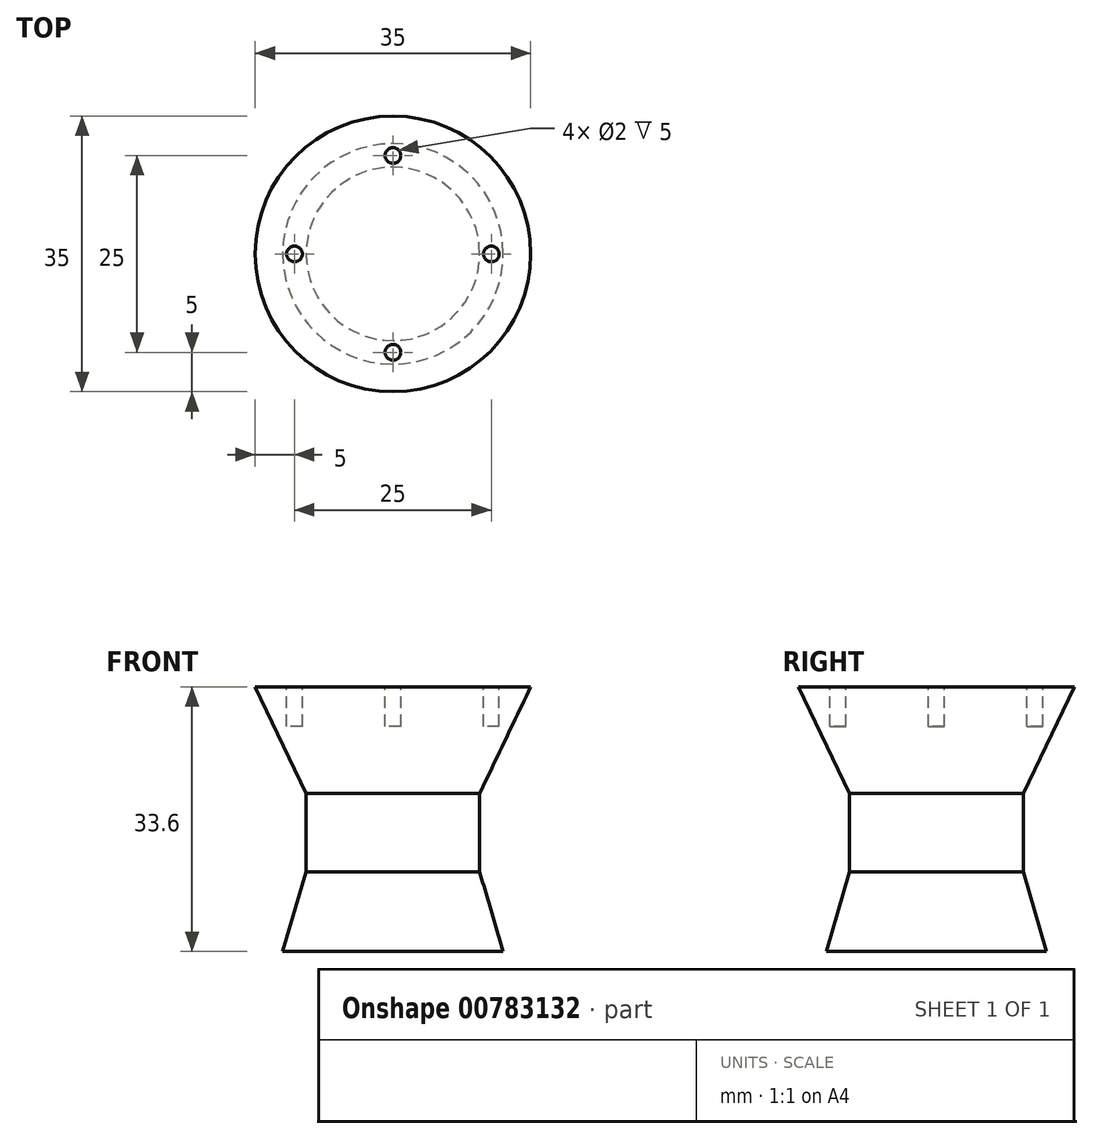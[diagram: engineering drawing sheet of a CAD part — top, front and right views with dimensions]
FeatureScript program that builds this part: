
annotation { "Feature Type Name" : "Feature", "Feature Type Description" : "" }
export const myFeature = defineFeature(function(context is Context, id is Id, definition is map)
    precondition{}
    {
        {
            var Q0;
            Q0=qCreatedBy(makeId("Front.planeOp"),FACE);
            var sketch = newSketch(context, id + "F0", { "sketchPlane" : qUnion([Q0])});
            skLineSegment(sketch, "E0", {"start": v(0, 0) * mm, "end": v(17.5, 0) * mm});
            skLineSegment(sketch, "E1", {"start": v(17.5, 0) * mm, "end": v(11.02, -13.53) * mm});
            skLineSegment(sketch, "E2", {"start": v(0, 0) * mm, "end": v(0, -13.53) * mm});
            skLineSegment(sketch, "E3", {"start": v(0, -13.53) * mm, "end": v(11.02, -13.53) * mm});
            skSolve(sketch);
        }
        {
            var Q0;
            Q0=makeQuery(id+"F0.imprint","IMPRINT",FACE,{"disambiguationData":[TD([[makeQuery(id+"F0.imprint","IMPRINT",EDGE,{"derivedFrom":sQuery(id+"F0.wireOp",EDGE,"E0")}),-1.0]])]});
            var Q1;
            Q1=sQuery(id+"F0.wireOp",EDGE,"E2");
            revolve(context, id + "F1", {"surfaceOperationType" : NewSurfaceOperationType.NEW, "entities" : qUnion([Q0]), "axis" : qUnion([Q1]), "revolveType" : RevolveType.FULL});
        }
        {
            var Q0;
            Q0=makeQuery(id+"F1.opRevolve","SWEPT_FACE",FACE,{"disambiguationData":[OSD([sQuery(id+"F0.wireOp",EDGE,"E0")])]});
            var sketch = newSketch(context, id + "F2", { "sketchPlane" : qUnion([Q0])});
            skCircle(sketch, "E4", {"center": v(0, 0) * mm, "radius": 12.5 * mm, "construction": true});
            skLineSegment(sketch, "E5", {"start": v(-17.5, 0) * mm, "end": v(17.5, 0) * mm, "construction": true});
            skLineSegment(sketch, "E6", {"start": v(0, 17.5) * mm, "end": v(0, -17.5) * mm, "construction": true});
            skCircle(sketch, "E7", {"center": v(12.5, 0) * mm, "radius": 1 * mm});
            skCircle(sketch, "E8", {"center": v(0, 12.5) * mm, "radius": 1 * mm});
            skCircle(sketch, "E9", {"center": v(-12.5, 0) * mm, "radius": 1 * mm});
            skCircle(sketch, "E10", {"center": v(0, -12.5) * mm, "radius": 1 * mm});
            skSolve(sketch);
        }
        {
            var Q0;
            Q0=makeQuery(id+"F2.imprint","IMPRINT",FACE,{"disambiguationData":[TD([[makeQuery(id+"F2.imprint","IMPRINT",EDGE,{"derivedFrom":sQuery(id+"F2.wireOp",EDGE,"E8")}),1.0]])]});
            var Q1;
            Q1=makeQuery(id+"F2.imprint","IMPRINT",FACE,{"disambiguationData":[TD([[makeQuery(id+"F2.imprint","IMPRINT",EDGE,{"derivedFrom":sQuery(id+"F2.wireOp",EDGE,"E9")}),1.0]])]});
            var Q2;
            Q2=makeQuery(id+"F2.imprint","IMPRINT",FACE,{"disambiguationData":[TD([[makeQuery(id+"F2.imprint","IMPRINT",EDGE,{"derivedFrom":sQuery(id+"F2.wireOp",EDGE,"E7")}),1.0]])]});
            var Q3;
            Q3=makeQuery(id+"F2.imprint","IMPRINT",FACE,{"disambiguationData":[TD([[makeQuery(id+"F2.imprint","IMPRINT",EDGE,{"derivedFrom":sQuery(id+"F2.wireOp",EDGE,"E10")}),1.0]])]});
            extrude(context, id + "F3", {"entities" : qUnion([Q0, Q1, Q2, Q3]), "operationType" : NewBodyOperationType.REMOVE, "oppositeDirection" : true, "depth" : 5 * mm, "offsetDistance" : 25 * mm});
        }
        {
            var Q0;
            Q0=makeQuery(id+"F1.opRevolve","SWEPT_FACE",FACE,{"disambiguationData":[OSD([sQuery(id+"F0.wireOp",EDGE,"E3")])]});
            var sketch = newSketch(context, id + "F4", { "sketchPlane" : qUnion([Q0])});
            skCircle(sketch, "E11", {"center": v(0, 0) * mm, "radius": 11.02 * mm});
            skSolve(sketch);
        }
        {
            var Q0;
            Q0=makeQuery(id+"F4.imprint","IMPRINT",FACE,{"disambiguationData":[TD([[makeQuery(id+"F4.imprint","IMPRINT",EDGE,{"derivedFrom":sQuery(id+"F4.wireOp",EDGE,"E11")}),-1.0]])]});
            extrude(context, id + "F5", {"entities" : qUnion([Q0]), "operationType" : NewBodyOperationType.ADD, "depth" : 10 * mm, "offsetDistance" : 25 * mm});
        }
        {
            var Q0;
            Q0=qCreatedBy(makeId("Front.planeOp"),FACE);
            var sketch = newSketch(context, id + "F6", { "sketchPlane" : qUnion([Q0])});
            skLineSegment(sketch, "E12.0", {"start": v(-11.02, -23.53) * mm, "end": v(11.02, -23.53) * mm});
            skLineSegment(sketch, "E13", {"start": v(0, -23.53) * mm, "end": v(0, -33.6) * mm});
            skLineSegment(sketch, "E14", {"start": v(0, -33.6) * mm, "end": v(-14, -33.6) * mm});
            skLineSegment(sketch, "E15", {"start": v(-14, -33.6) * mm, "end": v(-11.02, -23.53) * mm});
            skSolve(sketch);
        }
        {
            var Q0;
            {var subQ2=sQuery(id+"F6.wireOp",EDGE,"E13");Q0=makeQuery(id+"F6.imprint","IMPRINT",FACE,{"disambiguationData":[TD([[makeQuery(id+"F6.imprint","IMPRINT",EDGE,{"derivedFrom":subQ2}),-1.0]])]});}
            var Q1;
            Q1=sQuery(id+"F6.wireOp",EDGE,"E13");
            revolve(context, id + "F7", {"operationType" : NewBodyOperationType.ADD, "surfaceOperationType" : NewSurfaceOperationType.NEW, "entities" : qUnion([Q0]), "axis" : qUnion([Q1]), "revolveType" : RevolveType.FULL});
        }
    });
